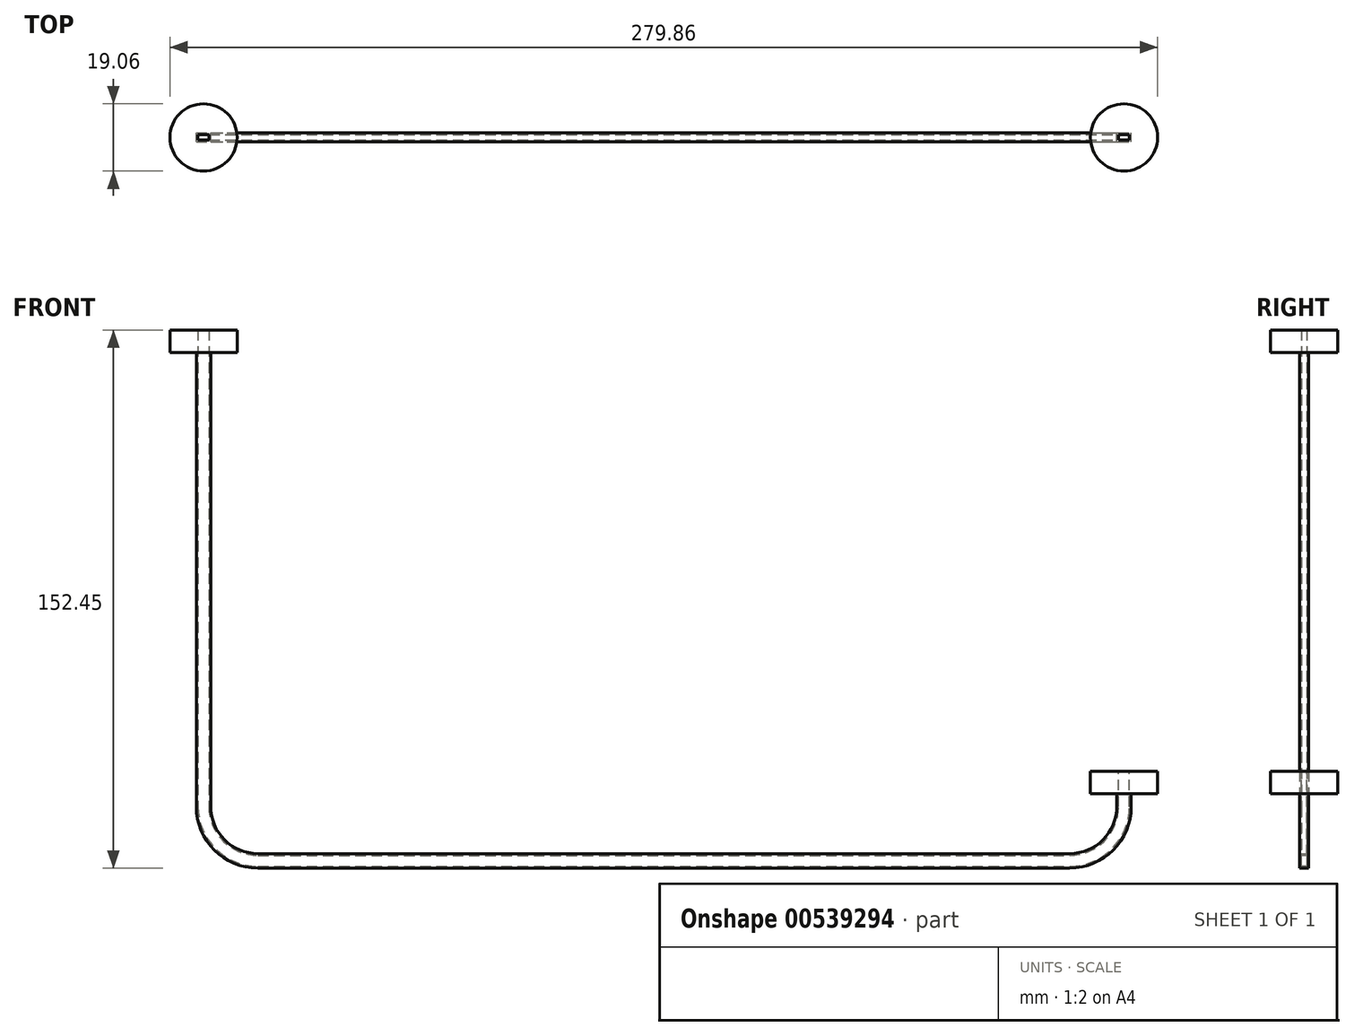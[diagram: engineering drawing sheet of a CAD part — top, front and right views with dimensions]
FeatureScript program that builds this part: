
annotation { "Feature Type Name" : "Feature", "Feature Type Description" : "" }
export const myFeature = defineFeature(function(context is Context, id is Id, definition is map)
    precondition{}
    {
        {
            var Q0;
            Q0=qCreatedBy(makeId("Front.planeOp"),FACE);
            var sketch = newSketch(context, id + "F0", { "sketchPlane" : qUnion([Q0])});
            skLineSegment(sketch, "E0", {"start": v(0, 0) * mm, "end": v(0, -10) * mm});
            skLineSegment(sketch, "E1", {"start": v(-25.4, -25.4) * mm, "end": v(-235.4, -25.4) * mm});
            skLineSegment(sketch, "E2", {"start": v(0, 0) * mm, "end": v(-25.4, 0) * mm});
            skLineSegment(sketch, "E3", {"start": v(-25.4, 0) * mm, "end": v(-25.4, -25.4) * mm});
            skLineSegment(sketch, "E4", {"start": v(-25.4, -25.4) * mm, "end": v(-15.4, -25.4) * mm});
            skArc(sketch, "E5", {"start": v(-15.4, -25.4) * mm, "mid": v(-4.51, -20.89) * mm, "end": v(0, -10) * mm});
            skLineSegment(sketch, "E6", {"start": v(-235.4, -25.4) * mm, "end": v(-235.4, 0) * mm});
            skLineSegment(sketch, "E7", {"start": v(-260.8, 0) * mm, "end": v(-235.4, 0) * mm});
            skLineSegment(sketch, "E8", {"start": v(-235.4, -25.4) * mm, "end": v(-245.4, -25.4) * mm});
            skLineSegment(sketch, "E9", {"start": v(-260.8, 0) * mm, "end": v(-260.8, -10) * mm});
            skArc(sketch, "E10", {"start": v(-260.8, -10) * mm, "mid": v(-256.29, -20.89) * mm, "end": v(-245.4, -25.4) * mm});
            skLineSegment(sketch, "E11", {"start": v(-260.8, 0) * mm, "end": v(-260.8, 125) * mm});
            skSolve(sketch);
        }
        {
            var Q0;
            Q0=qCreatedBy(makeId("Top.planeOp"),FACE);
            var sketch = newSketch(context, id + "F1", { "sketchPlane" : qUnion([Q0])});
            skLineSegment(sketch, "E12.bottom", {"start": v(-1.55, -0.78) * mm, "end": v(1.55, -0.78) * mm});
            skLineSegment(sketch, "E12.top", {"start": v(-1.55, 0.77) * mm, "end": v(1.55, 0.77) * mm});
            skLineSegment(sketch, "E12.left", {"start": v(-1.55, -0.78) * mm, "end": v(-1.55, 0.77) * mm});
            skLineSegment(sketch, "E12.right", {"start": v(1.55, -0.78) * mm, "end": v(1.55, 0.77) * mm});
            skPoint(sketch, "E12.middle", {"position": v(0, 0) * mm});
            skLineSegment(sketch, "E13.bottom", {"start": v(-2.05, -1.27) * mm, "end": v(2.05, -1.27) * mm});
            skLineSegment(sketch, "E13.top", {"start": v(-2.05, 1.27) * mm, "end": v(2.05, 1.27) * mm});
            skLineSegment(sketch, "E13.left", {"start": v(-2.05, -1.27) * mm, "end": v(-2.05, 1.27) * mm});
            skLineSegment(sketch, "E13.right", {"start": v(2.05, -1.27) * mm, "end": v(2.05, 1.27) * mm});
            skCircle(sketch, "E14", {"center": v(0, 0) * mm, "radius": 9.53 * mm});
            skSolve(sketch);
        }
        {
            var Q0;
            Q0=qCreatedBy(makeId("Top.planeOp"),FACE);
            cPlane(context, id + "F2", {"entities" : qUnion([Q0]), "cplaneType" : CPlaneType.OFFSET, "offset" : 125 * mm, "width" : 150 * mm, "height" : 150 * mm});
        }
        {
            var Q0;
            Q0=qCreatedBy(id+"F2.planeOp",FACE);
            var sketch = newSketch(context, id + "F3", { "sketchPlane" : qUnion([Q0])});
            skLineSegment(sketch, "E15.bottom", {"start": v(-262.35, 0.78) * mm, "end": v(-259.25, 0.78) * mm});
            skLineSegment(sketch, "E15.top", {"start": v(-262.35, -0.77) * mm, "end": v(-259.25, -0.77) * mm});
            skLineSegment(sketch, "E15.left", {"start": v(-262.35, 0.78) * mm, "end": v(-262.35, -0.77) * mm});
            skLineSegment(sketch, "E15.right", {"start": v(-259.25, 0.78) * mm, "end": v(-259.25, -0.77) * mm});
            skPoint(sketch, "E15.middle", {"position": v(-260.8, 0) * mm});
            skLineSegment(sketch, "E16.bottom", {"start": v(-262.85, -1.28) * mm, "end": v(-258.75, -1.28) * mm});
            skLineSegment(sketch, "E16.top", {"start": v(-262.85, 1.27) * mm, "end": v(-258.75, 1.27) * mm});
            skLineSegment(sketch, "E16.left", {"start": v(-262.85, -1.28) * mm, "end": v(-262.85, 1.27) * mm});
            skLineSegment(sketch, "E16.right", {"start": v(-258.75, -1.28) * mm, "end": v(-258.75, 1.27) * mm});
            skCircle(sketch, "E17", {"center": v(-260.8, 0) * mm, "radius": 9.53 * mm});
            skSolve(sketch);
        }
        {
            var Q0;
            Q0=makeQuery(id+"F3.imprint","IMPRINT",FACE,{"disambiguationData":[TD([[makeQuery(id+"F3.imprint","IMPRINT",EDGE,{"derivedFrom":sQuery(id+"F3.wireOp",EDGE,"E15.bottom")}),1.0]])]});
            var Q1;
            Q1=sQuery(id+"F0.wireOp",EDGE,"E11");
            var Q2;
            Q2=sQuery(id+"F0.wireOp",EDGE,"E9");
            var Q3;
            Q3=sQuery(id+"F0.wireOp",EDGE,"E10");
            var Q4;
            Q4=sQuery(id+"F0.wireOp",EDGE,"E8");
            var Q5;
            Q5=sQuery(id+"F0.wireOp",EDGE,"E1");
            var Q6;
            Q6=sQuery(id+"F0.wireOp",EDGE,"E4");
            var Q7;
            Q7=sQuery(id+"F0.wireOp",EDGE,"E5");
            var Q8;
            Q8=sQuery(id+"F0.wireOp",EDGE,"E0");
            sweep(context, id + "F4", {"profiles" : qUnion([Q0]), "path" : qUnion([Q1, Q2, Q3, Q4, Q5, Q6, Q7, Q8])});
        }
        {
            var Q0;
            Q0=makeQuery(id+"F3.imprint","IMPRINT",FACE,{"disambiguationData":[TD([[makeQuery(id+"F3.imprint","IMPRINT",EDGE,{"derivedFrom":sQuery(id+"F3.wireOp",EDGE,"E16.bottom")}),-1.0]])]});
            extrude(context, id + "F5", {"entities" : qUnion([Q0]), "operationType" : NewBodyOperationType.ADD, "oppositeDirection" : true, "depth" : 6.35 * mm, "offsetDistance" : 25 * mm});
        }
        {
            var Q0;
            Q0=makeQuery(id+"F1.imprint","IMPRINT",FACE,{"disambiguationData":[TD([[makeQuery(id+"F1.imprint","IMPRINT",EDGE,{"derivedFrom":sQuery(id+"F1.wireOp",EDGE,"E13.bottom")}),-1.0]])]});
            extrude(context, id + "F6", {"entities" : qUnion([Q0]), "operationType" : NewBodyOperationType.ADD, "oppositeDirection" : true, "depth" : 6.35 * mm, "offsetDistance" : 25 * mm});
        }
    });
